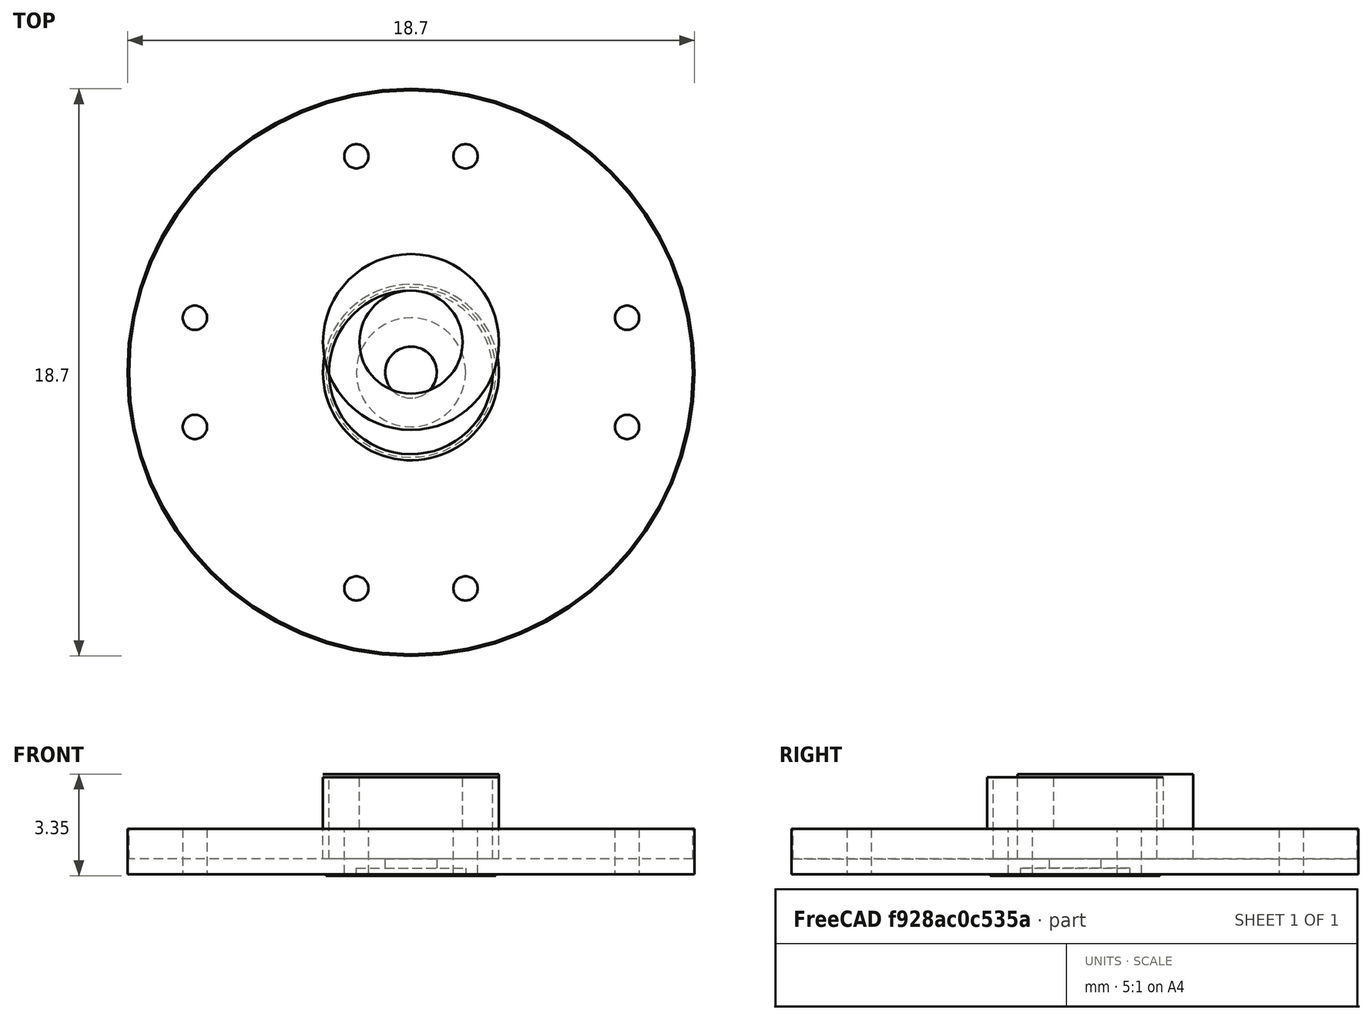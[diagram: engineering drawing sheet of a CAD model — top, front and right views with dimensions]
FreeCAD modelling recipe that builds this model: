
FCSTD DOCUMENT  (FreeCAD 0.16R6712 (Git))
Label: horn
License: All rights reserved
LicenseURL: http://en.wikipedia.org/wiki/All_rights_reserved
objects: Part::Cylinder×8, Part::Cut×6, Part::FeaturePython×1, Part::MultiFuse×1
note: 16 computed .brp shape members not serialized (recipe doc carries the construction recipe); baked Part::Feature solids carry a one-line shape summary decoded from their .brp

FEATURE [Part::FeaturePython] Clone187  label="Clone of horn"  # WARN: FeaturePython — macro-defined, semantics opaque (R4)
  Placement = pos=(0,0,0) rot=(0,1,0;3.14159rad)
  Scale = (1,1,1)
FEATURE [Part::Cylinder] Cylinder  label="Cilindro"
  Angle = 360
  Height = 1
  Placement = pos=(0,0,-1) rot=(0,0,1;0rad)
  Radius = 9.3
FEATURE [Part::Cylinder] Cylinder001  label="Cilindro001"
  Angle = 360
  Height = 1.8
  Radius = 2.9
FEATURE [Part::Cylinder] Cylinder002  label="Cilindro002"
  Angle = 360
  Height = 6
  Placement = pos=(0,0,-3) rot=(0,0,1;0rad)
  Radius = 1.7
FEATURE [Part::Cut] Cut
  Base = -> Cylinder001
  Placement = pos=(0,1,0) rot=(0,0,1;0rad)
  Tool = -> Cylinder002
FEATURE [Part::Cylinder] Cylinder003  label="Cilindro003"
  Angle = 360
  Height = 7.8
  Radius = 2.9
FEATURE [Part::Cylinder] Cylinder004  label="Cilindro004"
  Angle = 360
  Height = 10
  Placement = pos=(0,0,-3) rot=(0,0,1;0rad)
  Radius = 1.7
FEATURE [Part::Cut] Cut001
  Base = -> Cylinder003
  Placement = pos=(0,1,-4) rot=(0,0,1;0rad)
  Tool = -> Cylinder004
FEATURE [Part::Cut] Cut002
  Base = -> Cylinder
  Tool = -> Cut001
FEATURE [Part::Cylinder] Cylinder005  label="Cilindro005"
  Angle = 360
  Height = 10
  Placement = pos=(0,1,-4) rot=(0,0,1;0rad)
  Radius = 2
FEATURE [Part::Cut] Cut003
  Base = -> Cut002
  Tool = -> Cylinder005
FEATURE [Part::MultiFuse] Fusion
  Shapes = -> [Cut,Cut003]
FEATURE [Part::Cylinder] Cylinder006  label="Cilindro006"
  Angle = 360
  Height = 12
  Placement = pos=(0,0,-1) rot=(0,0,1;0rad)
  Radius = 2.7
FEATURE [Part::Cut] Cut004
  Base = -> Clone187
  Tool = -> Cylinder006
FEATURE [Part::Cylinder] Cylinder007  label="Cilindro007"
  Angle = 360
  Height = 10.45
  Placement = pos=(0,0,-12) rot=(0,0,1;0rad)
  Radius = 5
FEATURE [Part::Cut] Cut005
  Base = -> Cut004
  Tool = -> Cylinder007
